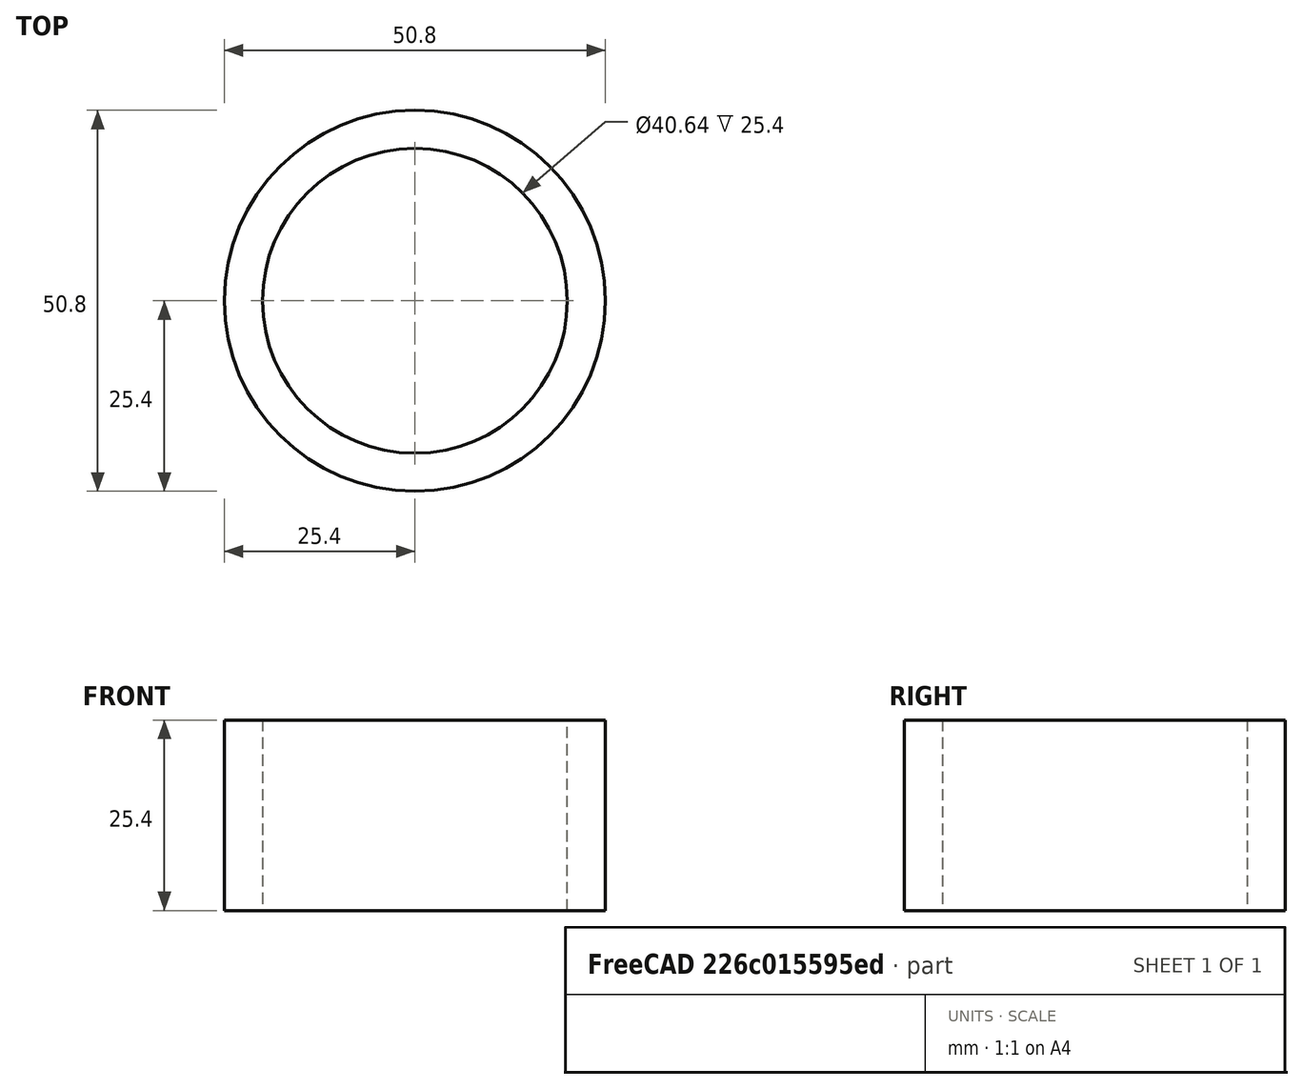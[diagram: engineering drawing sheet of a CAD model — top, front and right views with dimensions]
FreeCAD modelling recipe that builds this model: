
FCSTD DOCUMENT  (FreeCAD 0.19R24291 (Git))
Label: AdaptCardboardTube
License: All rights reserved
LicenseURL: http://en.wikipedia.org/wiki/All_rights_reserved
objects: Sketcher::SketchObject×1, PartDesign::Pad×1, PartDesign::Body×1
note: 4 computed .brp shape members not serialized (recipe doc carries the construction recipe); baked Part::Feature solids carry a one-line shape summary decoded from their .brp

FEATURE [Sketcher::SketchObject] Sketch
  FullyConstrained = true
  MapMode = 5
  Support = -> [XY_Plane]
  sketch-geometry (2):
    g0: Circle CenterX=0 CenterY=0 CenterZ=0 NormalX=0 NormalY=0 NormalZ=1 AngleXU=0 Radius=25.4
    g1: Circle CenterX=0 CenterY=0 CenterZ=0 NormalX=0 NormalY=0 NormalZ=1 AngleXU=0 Radius=20.32
  constraints (4):
    c: Coincident(g0,g-1)
    c: Coincident(g1,g0)
    c: Diameter(g0) = 50.8
    c: Diameter(g1) = 40.64
FEATURE [PartDesign::Pad] Pad
  Direction = (1,1,1)
  Length = 25.4
  Length2 = 99.9998
  Profile = -> Sketch
  Type = 0
FEATURE [PartDesign::Body] Body
  Group = -> [Sketch,Pad]
  Origin = -> Origin
  Tip = -> Pad
